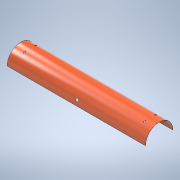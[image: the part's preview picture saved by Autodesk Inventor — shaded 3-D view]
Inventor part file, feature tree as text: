
AUTODESK INVENTOR PART (.ipt)
format: ipt  version: 2022 (Build 260153000, 153)  size: 150,528 bytes
history: native  units: mm
features: sketch x3, hole x2, extrude x1, plane x1, projected_geometry x1
ambient origin geometry x8: Origin, YZ Plane, XZ Plane, XY Plane, X Axis, Y Axis, Z Axis, Center Point
bodies: Solid1 (feature_tree)
feature tree (8):
  extrude  "Extrusion1"  Depth=59.6mm
  hole  "Hole1"  [1 undecoded]
  plane  "Work Plane1"
  hole  "Hole2"  [1 undecoded]
  sketch  "Sketch1"  dims[d0=29.8mm d1=59.6mm]
  sketch  "Sketch2"  dims[d4=29.48mm d5=300.0mm d6=0.0mm]
  projected_geometry  "Projected Loop1"
  sketch  "Sketch3"  dims[d7=10.0mm d8=5.4mm d9=6.0mm d10=4.0mm d11=2.0mm d12=90.0deg d13=8.0mm d14=20.594885mm d16=20.0mm d17=27.0mm d19=260.0mm d20=2.0mm d21=6.0mm d22=4.0mm d23=2.0mm d24=90.0deg d25=8.0mm d26=20.594885mm]
note: 2 required parameter values undecoded (feature->parameter linkage not recoverable at this tier; creation-order binding heuristic only, values carry confidence <= 0.55)
